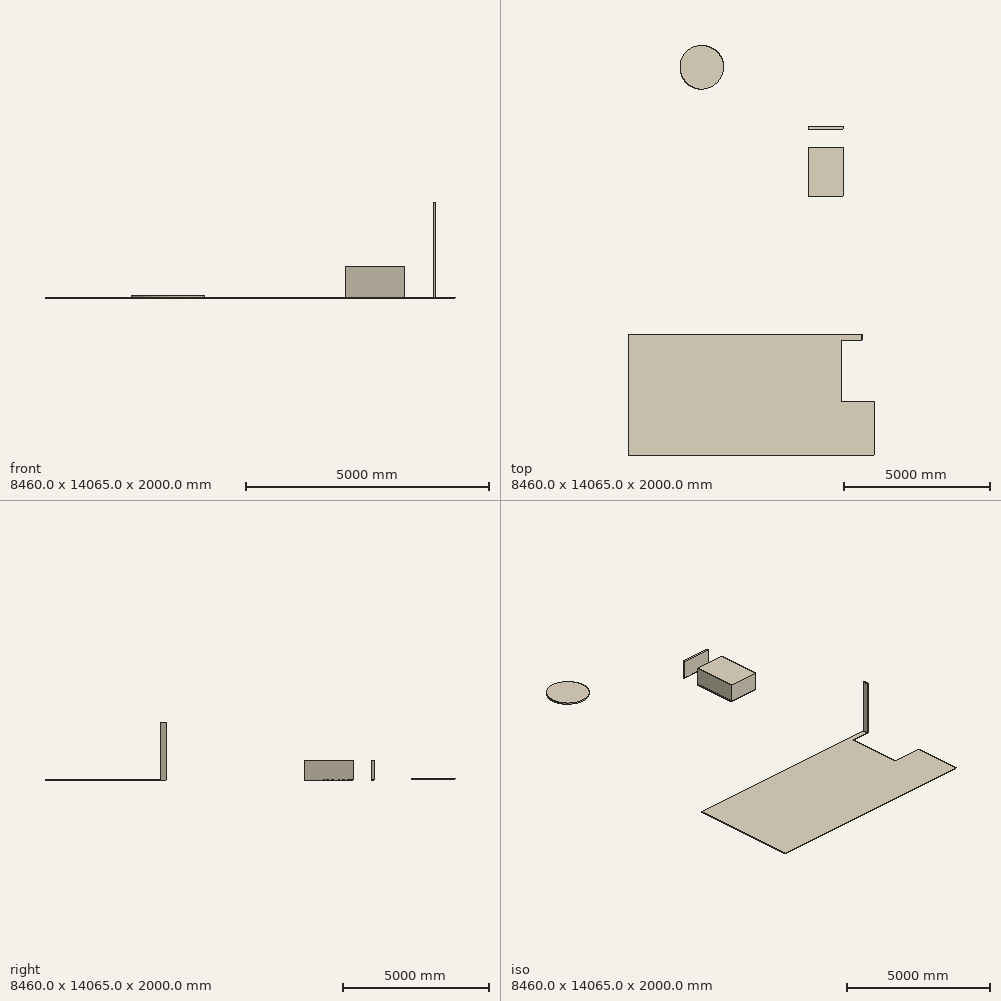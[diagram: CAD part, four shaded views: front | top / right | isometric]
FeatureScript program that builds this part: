
annotation { "Feature Type Name" : "Feature", "Feature Type Description" : "" }
export const myFeature = defineFeature(function(context is Context, id is Id, definition is map)
    precondition{}
    {
        {
            var Q0;
            Q0=qCreatedBy(makeId("Top.planeOp"),FACE);
            var sketch = newSketch(context, id + "F0", { "sketchPlane" : qUnion([Q0])});
            skLineSegment(sketch, "E0", {"start": v(3786.2, -11769.83) * mm, "end": v(3786.2, -9919.83) * mm});
            skLineSegment(sketch, "E1", {"start": v(3786.2, -9919.83) * mm, "end": v(2626.2, -9919.83) * mm});
            skLineSegment(sketch, "E2", {"start": v(2626.2, -9919.83) * mm, "end": v(2626.2, -7819.83) * mm});
            skLineSegment(sketch, "E3", {"start": v(2626.2, -7819.83) * mm, "end": v(3326.2, -7819.83) * mm});
            skLineSegment(sketch, "E4", {"start": v(3326.2, -7819.83) * mm, "end": v(3326.2, -619.83) * mm});
            skLineSegment(sketch, "E5", {"start": v(3326.2, -619.83) * mm, "end": v(-4673.8, -619.83) * mm});
            skLineSegment(sketch, "E6", {"start": v(-4673.8, -619.83) * mm, "end": v(-4673.8, -11769.83) * mm});
            skLineSegment(sketch, "E7", {"start": v(-4673.8, -11769.83) * mm, "end": v(3786.2, -11769.83) * mm});
            skLineSegment(sketch, "E8.bottom", {"start": v(2726.2, -1219.83) * mm, "end": v(1526.2, -1219.83) * mm});
            skLineSegment(sketch, "E8.top", {"start": v(2726.2, -3619.83) * mm, "end": v(1526.2, -3619.83) * mm});
            skLineSegment(sketch, "E8.left", {"start": v(2726.2, -1219.83) * mm, "end": v(2726.2, -3619.83) * mm});
            skLineSegment(sketch, "E8.right", {"start": v(1526.2, -1219.83) * mm, "end": v(1526.2, -3619.83) * mm});
            skLineSegment(sketch, "E9.bottom", {"start": v(2726.2, -492.67) * mm, "end": v(1526.2, -492.67) * mm});
            skLineSegment(sketch, "E9.top", {"start": v(2726.2, -2892.67) * mm, "end": v(1526.2, -2892.67) * mm});
            skLineSegment(sketch, "E9.left", {"start": v(2726.2, -492.67) * mm, "end": v(2726.2, -2892.67) * mm});
            skLineSegment(sketch, "E9.right", {"start": v(1526.2, -492.67) * mm, "end": v(1526.2, -2892.67) * mm});
            skLineSegment(sketch, "E10", {"start": v(-4673.8, -11769.83) * mm, "end": v(-4723.8, -11769.83) * mm});
            skLineSegment(sketch, "E11", {"start": v(-4723.8, -11769.83) * mm, "end": v(-4723.8, -569.83) * mm});
            skLineSegment(sketch, "E12", {"start": v(-4723.8, -569.83) * mm, "end": v(3376.2, -569.83) * mm});
            skLineSegment(sketch, "E13", {"start": v(3376.2, -569.83) * mm, "end": v(3376.2, -7819.83) * mm});
            skLineSegment(sketch, "E14", {"start": v(3326.2, -7819.83) * mm, "end": v(3376.2, -7819.83) * mm});
            skLineSegment(sketch, "E15", {"start": v(-4723.8, -11769.83) * mm, "end": v(-4723.8, -19894.83) * mm});
            skLineSegment(sketch, "E16", {"start": v(-4723.8, -19894.83) * mm, "end": v(-2573.8, -19894.83) * mm});
            skLineSegment(sketch, "E17", {"start": v(-2573.8, -19894.83) * mm, "end": v(-2573.8, -11769.83) * mm});
            skLineSegment(sketch, "E18", {"start": v(-4673.8, -7619.83) * mm, "end": v(3376.2, -7619.83) * mm});
            skSolve(sketch);
        }
        {
            var Q0;
            Q0=makeQuery(id+"F0.imprint","IMPRINT",FACE,{"disambiguationData":[TD([[makeQuery(id+"F0.imprint","IMPRINT",EDGE,{"derivedFrom":sQuery(id+"F0.wireOp",EDGE,"E9.bottom")}),1.0]])]});
            var Q1;
            Q1=makeQuery(id+"F0.imprint","IMPRINT",FACE,{"disambiguationData":[TD([[makeQuery(id+"F0.imprint","IMPRINT",EDGE,{"derivedFrom":sQuery(id+"F0.wireOp",EDGE,"E8.bottom")}),1.0]])]});
            var Q2;
            Q2=makeQuery(id+"F0.imprint","IMPRINT",FACE,{"disambiguationData":[TD([[makeQuery(id+"F0.imprint","IMPRINT",EDGE,{"derivedFrom":sQuery(id+"F0.wireOp",EDGE,"E0")}),1.0]])]});
            extrude(context, id + "F1", {"entities" : qUnion([Q0, Q1, Q2]), "depth" : 25 * mm, "offsetDistance" : 25 * mm});
        }
        {
            var Q0;
            Q0=makeQuery(id+"F0.imprint","IMPRINT",FACE,{"disambiguationData":[TD([[makeQuery(id+"F0.imprint","IMPRINT",EDGE,{"derivedFrom":sQuery(id+"F0.wireOp",EDGE,"E8.bottom")}),1.0]])]});
            var Q1;
            Q1=makeQuery(id+"F0.imprint","IMPRINT",FACE,{"disambiguationData":[TD([[makeQuery(id+"F0.imprint","IMPRINT",EDGE,{"derivedFrom":sQuery(id+"F0.wireOp",EDGE,"E9.bottom")}),1.0]])]});
            extrude(context, id + "F2", {"entities" : qUnion([Q0, Q1]), "depth" : 675 * mm, "offsetDistance" : 25 * mm});
        }
        {
            var Q0;
            Q0=makeQuery(id+"F0.imprint","IMPRINT",FACE,{"disambiguationData":[TD([[makeQuery(id+"F0.imprint","IMPRINT",EDGE,{"derivedFrom":sQuery(id+"F0.wireOp",EDGE,"E4")}),-1.0]])]});
            extrude(context, id + "F3", {"entities" : qUnion([Q0]), "depth" : 2000 * mm, "offsetDistance" : 25 * mm});
        }
        {
            var Q0;
            Q0=makeQuery(id+"F1.opExtrude","CAP_FACE",FACE,{"disambiguationData":[OSD([sQuery(id+"F0.wireOp",EDGE,"E0"),sQuery(id+"F0.wireOp",EDGE,"E1"),sQuery(id+"F0.wireOp",EDGE,"E2"),sQuery(id+"F0.wireOp",EDGE,"E3"),sQuery(id+"F0.wireOp",EDGE,"E4"),sQuery(id+"F0.wireOp",EDGE,"E5"),sQuery(id+"F0.wireOp",EDGE,"E6"),sQuery(id+"F0.wireOp",EDGE,"E7")])],"isStart":false});
            var sketch = newSketch(context, id + "F4", { "sketchPlane" : qUnion([Q0])});
            skCircle(sketch, "E19", {"center": v(-2147.22, 1545.19) * mm, "radius": 750 * mm});
            skSolve(sketch);
        }
        {
            var Q0;
            Q0 = qSketchRegion(id + "F4", true);
            extrude(context, id + "F5", {"entities" : qUnion([Q0]), "depth" : 50 * mm, "offsetDistance" : 25 * mm});
        }
    });
